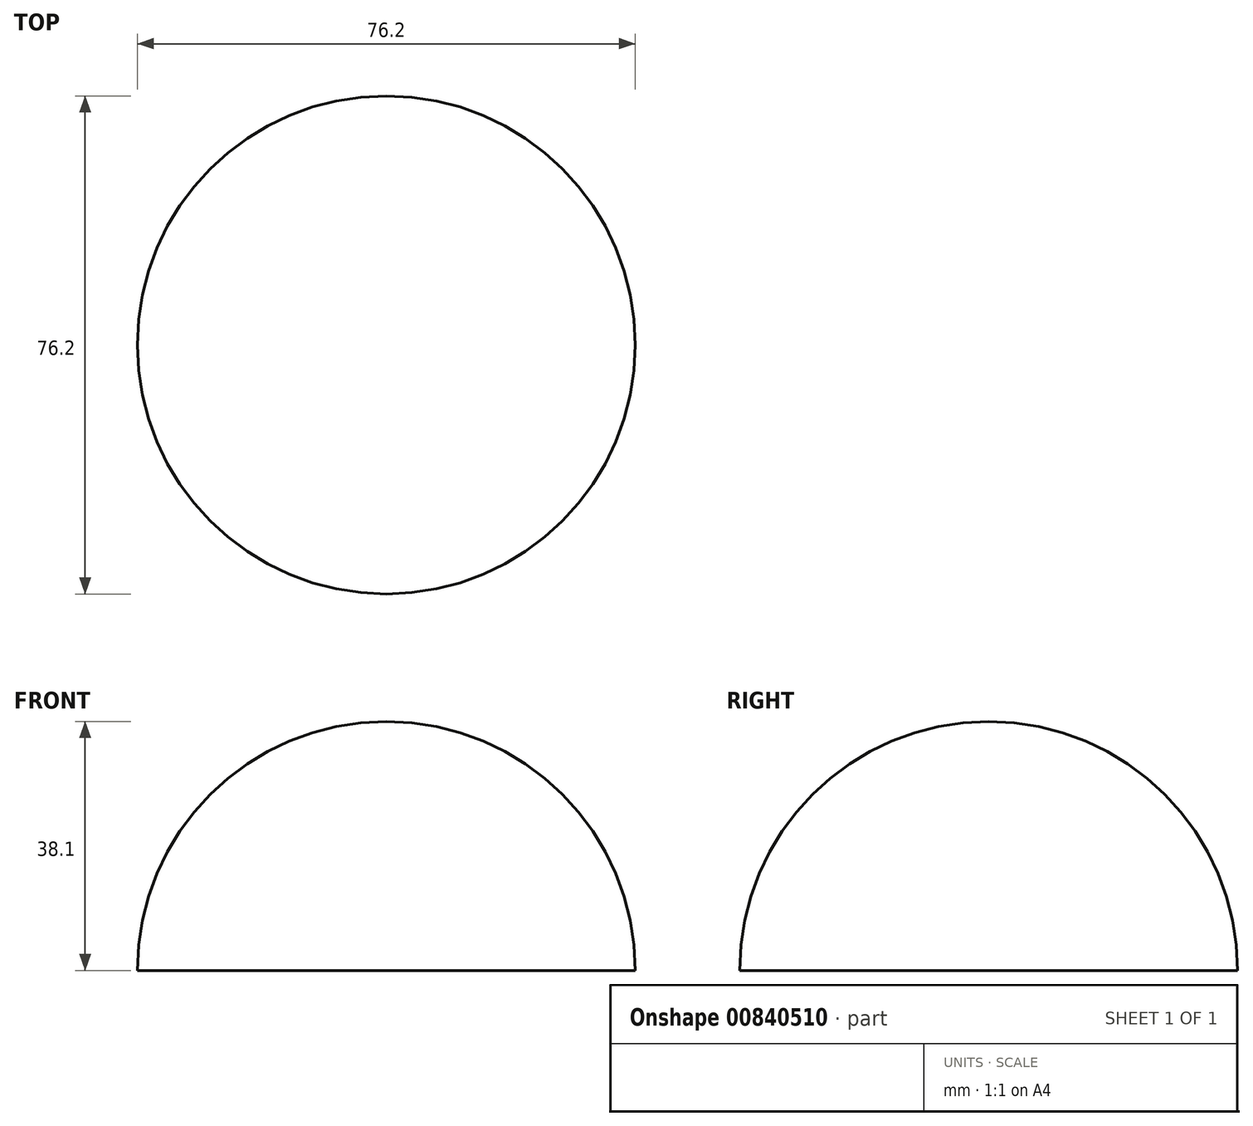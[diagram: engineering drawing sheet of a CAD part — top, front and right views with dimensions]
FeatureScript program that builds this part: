
annotation { "Feature Type Name" : "Feature", "Feature Type Description" : "" }
export const myFeature = defineFeature(function(context is Context, id is Id, definition is map)
    precondition{}
    {
        {
            var Q0;
            Q0=qCreatedBy(makeId("Top.planeOp"),FACE);
            var sketch = newSketch(context, id + "F0", { "sketchPlane" : qUnion([Q0])});
            skLineSegment(sketch, "E0", {"start": v(0, 76.2) * mm, "end": v(0, 0) * mm});
            skArc(sketch, "E1", {"start": v(0, 0) * mm, "mid": v(38.1, 38.1) * mm, "end": v(0, 76.2) * mm});
            skSolve(sketch);
        }
        {
            var Q0;
            Q0 = qSketchRegion(id + "F0", true);
            var Q1;
            Q1=sQuery(id+"F0.wireOp",EDGE,"E0");
            revolve(context, id + "F1", {"surfaceOperationType" : NewSurfaceOperationType.NEW, "entities" : qUnion([Q0]), "axis" : qUnion([Q1]), "revolveType" : RevolveType.ONE_DIRECTION, "angle" : 180 * degree});
        }
    });
